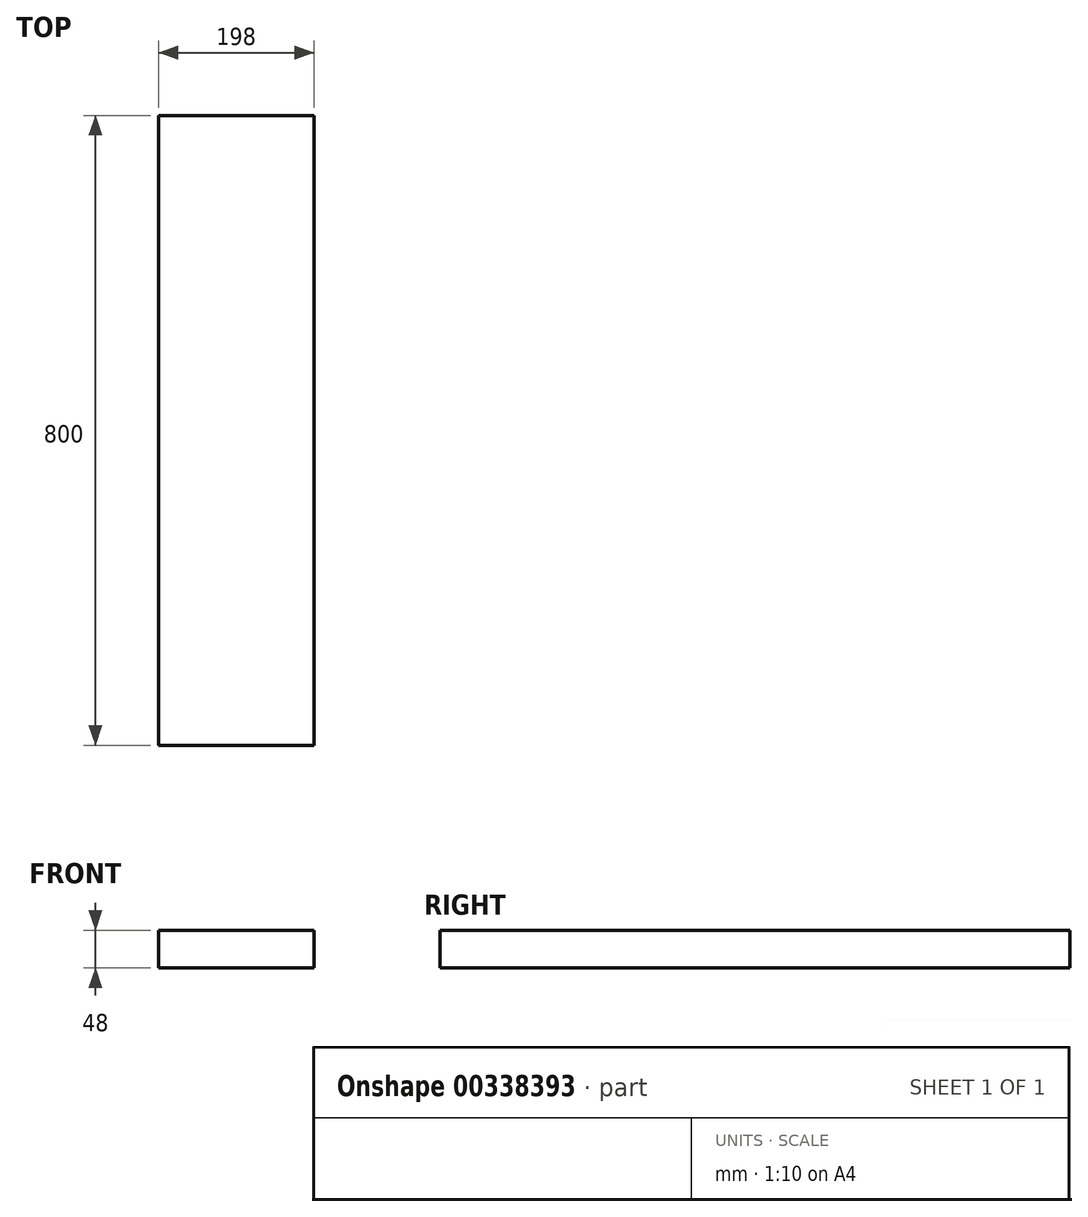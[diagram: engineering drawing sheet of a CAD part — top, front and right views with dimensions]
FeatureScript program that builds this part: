
annotation { "Feature Type Name" : "Feature", "Feature Type Description" : "" }
export const myFeature = defineFeature(function(context is Context, id is Id, definition is map)
    precondition{}
    {
        {
            var Q0;
            Q0=qCreatedBy(makeId("Front.planeOp"),FACE);
            var sketch = newSketch(context, id + "F0", { "sketchPlane" : qUnion([Q0])});
            skLineSegment(sketch, "E0.bottom", {"start": v(-99, -24) * mm, "end": v(99, -24) * mm});
            skLineSegment(sketch, "E0.top", {"start": v(-99, 24) * mm, "end": v(99, 24) * mm});
            skLineSegment(sketch, "E0.left", {"start": v(-99, -24) * mm, "end": v(-99, 24) * mm});
            skLineSegment(sketch, "E0.right", {"start": v(99, -24) * mm, "end": v(99, 24) * mm});
            skPoint(sketch, "E0.middle", {"position": v(0, 0) * mm});
            skSolve(sketch);
        }
        {
            var Q0;
            Q0=makeQuery(id+"F0.imprint","IMPRINT",FACE,{"disambiguationData":[TD([[makeQuery(id+"F0.imprint","IMPRINT",EDGE,{"derivedFrom":sQuery(id+"F0.wireOp",EDGE,"E0.bottom")}),1.0]])]});
            extrude(context, id + "F1", {"entities" : qUnion([Q0]), "depth" : 800 * mm});
        }
    });
